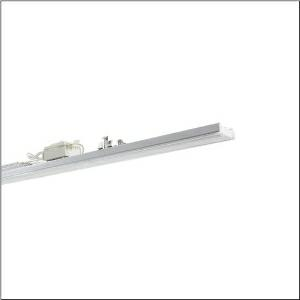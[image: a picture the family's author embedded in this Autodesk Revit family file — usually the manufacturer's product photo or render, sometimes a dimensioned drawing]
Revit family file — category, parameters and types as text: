
# Revit family: licross_r__21_recessed_ho_51te12vn4axm_dc7e
name_source: partatom
category: Lighting Fixtures
units: mm (PartAtom-declared; Revit-internal decimal feet)

## family parameters
Cut with Voids When Loaded = No
Host = Face
Light Source = No
Part Type = Normal
Room Calculation Point = No
Round Connector Dimension = Use Diameter
Shared = No

## types (1)
- --- (1 x LED, 10000 lm, 53.4 W, 4000K)
    Apparent Load = 53 VA
    CIE Flux Codes = 66 91 98 100 100
    Color Rendering = 80
    Color Temperature = 4000K
    Default Elevation = 1800 mm
    Description = Licross® 21 Recessed HO, luminaire insert, of sheet steel, galvanised, coil coated, white, length: 1.500mm, width: 66mm, height: 67mm, LED rated luminous flux: 10.000lm, light colour: 840, control gear: DALI 2, CLO, with plug, 5-pole, with phase selection, mains connection: 220..240V, AC, 50/60Hz, start of lifetime: 53W, end of service life: 59W, internal wiring halogen-free, primary optical cover: cover, of PMMA, light emission: direct distribution, primary light characteristic: symmetric, protection rating (complete): IP54, insulation class (complete): insulation class I (protective earthing), certification: CE, ENEC, VDE, UKCA, protection symbol: D if used in an environment with non-conductive dust loads with corresponding accessories, impact resistance: IK06, permissible ambient temperature for indoor applications: -25..+35°C, corresponds to IFS (International Featured Standards) requirements for safety and quality in the food industry, reducing of maximum allowable ambient temperature of 5°C with ceiling mounting, LABS conformity tested according to VDMA 24364:2018-05, packaging unit: 1 piece
    Height = 58 mm
    Lamp = 1 x LED
    Lamp Light Flux = 10000 lm
    Lamp Power = 53.4 W
    Lamp count = 1
    Length = 1500 mm
    Luminous efficacy = 187 lm/W
    Manufacturer = Siteco
    ModVariant = No
    Model = 51TE12VN4AXM
    Mounting Place = Ceiling
    Mounting Type = Pendant
    Number of Poles = 1
    OnlyDefault = Yes
    Power Factor = 1
    Product Name = Licross® 21 Recessed HO
    Product group = luminaire insert | ceiling pendant
    ProductGroupID = 902
    Protection Class = Protection class I
    Protection Degree = IP 54
    RLX_Detail_Level = 1
    RLX_Emergency_Light_Flux = 0 lm
    RLX_Emergency_Type = 0
    RLX_Emergency_Type_DB = No
    RlxData = <blob elided: 24561 chars, md5=8fd11184>
    Socket = socket
    Standby Power = 0 W
    System Light Flux = 10000 lm
    System Power = 53 W
    Type Comments = factory setting: luminous flux: 100 % | dim-lin: 254 | 364 mA
    Type Image = l_1296930.jpg
    URL = http://relux.com
    VarID = @adj_108733
    Voltage = 0 V
    Weight = 0.00 kg
    Width = 66 mm

## geometry (parser evidence)
native form markers: Blend x4, Sweep x12
no freeform markers — native parametric forms only
